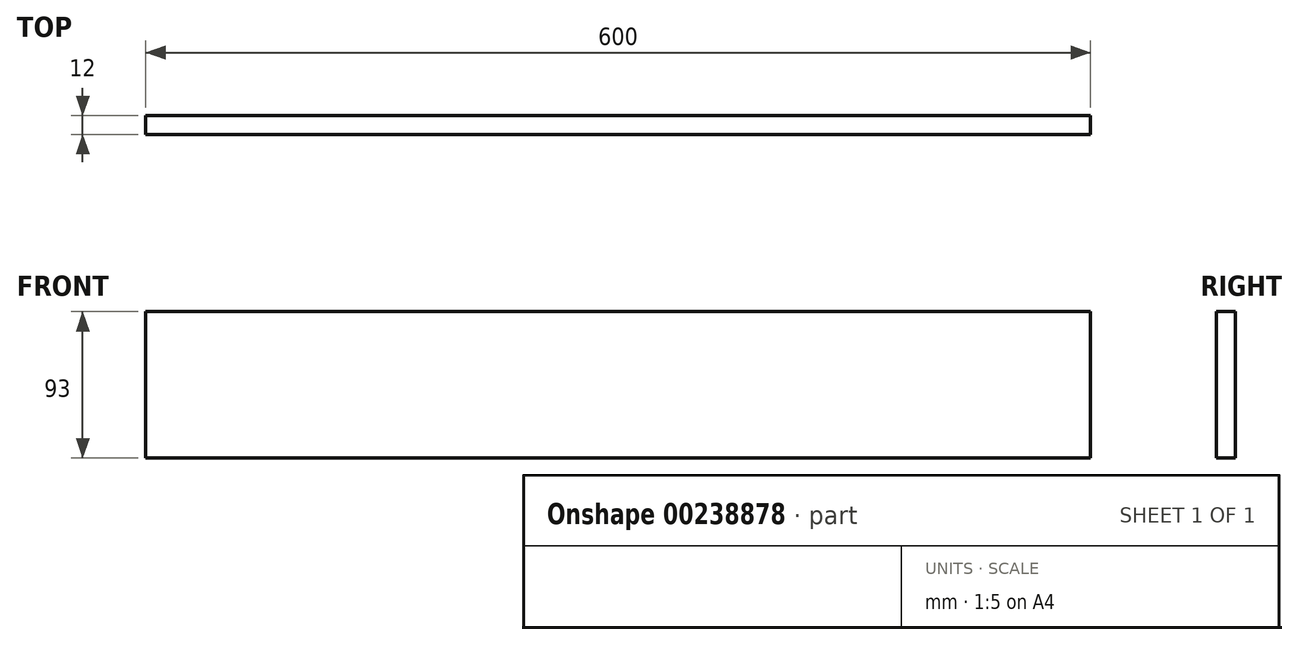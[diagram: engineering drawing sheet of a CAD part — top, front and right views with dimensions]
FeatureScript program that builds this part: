
annotation { "Feature Type Name" : "Feature", "Feature Type Description" : "" }
export const myFeature = defineFeature(function(context is Context, id is Id, definition is map)
    precondition{}
    {
        {
            var Q0;
            Q0=qCreatedBy(makeId("Front.planeOp"),FACE);
            var sketch = newSketch(context, id + "F0", { "sketchPlane" : qUnion([Q0])});
            skLineSegment(sketch, "E0.bottom", {"start": v(0, 0) * mm, "end": v(600, 0) * mm});
            skLineSegment(sketch, "E0.top", {"start": v(0, 93) * mm, "end": v(600, 93) * mm});
            skLineSegment(sketch, "E0.left", {"start": v(0, 0) * mm, "end": v(0, 93) * mm});
            skLineSegment(sketch, "E0.right", {"start": v(600, 0) * mm, "end": v(600, 93) * mm});
            skSolve(sketch);
        }
        {
            var Q0;
            Q0 = qSketchRegion(id + "F0", true);
            extrude(context, id + "F1", {"entities" : qUnion([Q0]), "offsetDistance" : 25 * mm, "depth" : 12 * mm});
        }
    });
